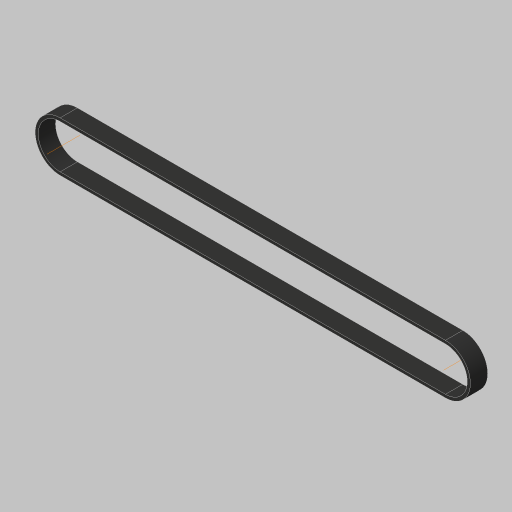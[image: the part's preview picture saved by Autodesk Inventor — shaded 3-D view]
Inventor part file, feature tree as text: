
AUTODESK INVENTOR PART (.ipt)
format: ipt  version: 2023.5 (Build 275446000, 446)  size: 158,208 bytes
history: native  units: in
note: dims shown in document units (in); Inventor stores cm internally (conversion verified against a paired STEP export)
features: sketch x3, extrude x1, other x1, projected_geometry x1
ambient origin geometry x8: Origin, YZ Plane, XZ Plane, XY Plane, X Axis, Y Axis, Z Axis, Center Point
bodies: Body1 (feature_tree)
feature tree (6):
  sketch  "Sketch2"  dims[d0=0.9023in d1=0.9023in]
  extrude  "Extrusion2"  Depth=0.9023in
  sketch  "Sketch5"  dims[d3=1.4174in d5=7.4409in d9=0.0787in d10=0.0598in d11=0.0299in d12=0.0219in d13=0.0219in d14=0.0059in d15=0.0059in d20=0.3346in d21=0.0in d22=0.0787in d23=0.0598in d24=0.0299in d25=0.0219in d26=0.0219in d27=0.0059in d28=0.0059in d29=0.0299in d30=0.0394in d31=0.0787in d32=0.0232in d34=0.0219in d35=0.0in d36=0.0in d37=0.0059in d38=0.0022in d39=0.0022in d40=0.0in d41=0.0in d42=0.0081in d43=0.0081in d44=0.0299in]
  other  "Work Axis1"
  sketch  "Sketch4"  dims[d2=1.4174in]
  projected_geometry  "Projected Loop1"
